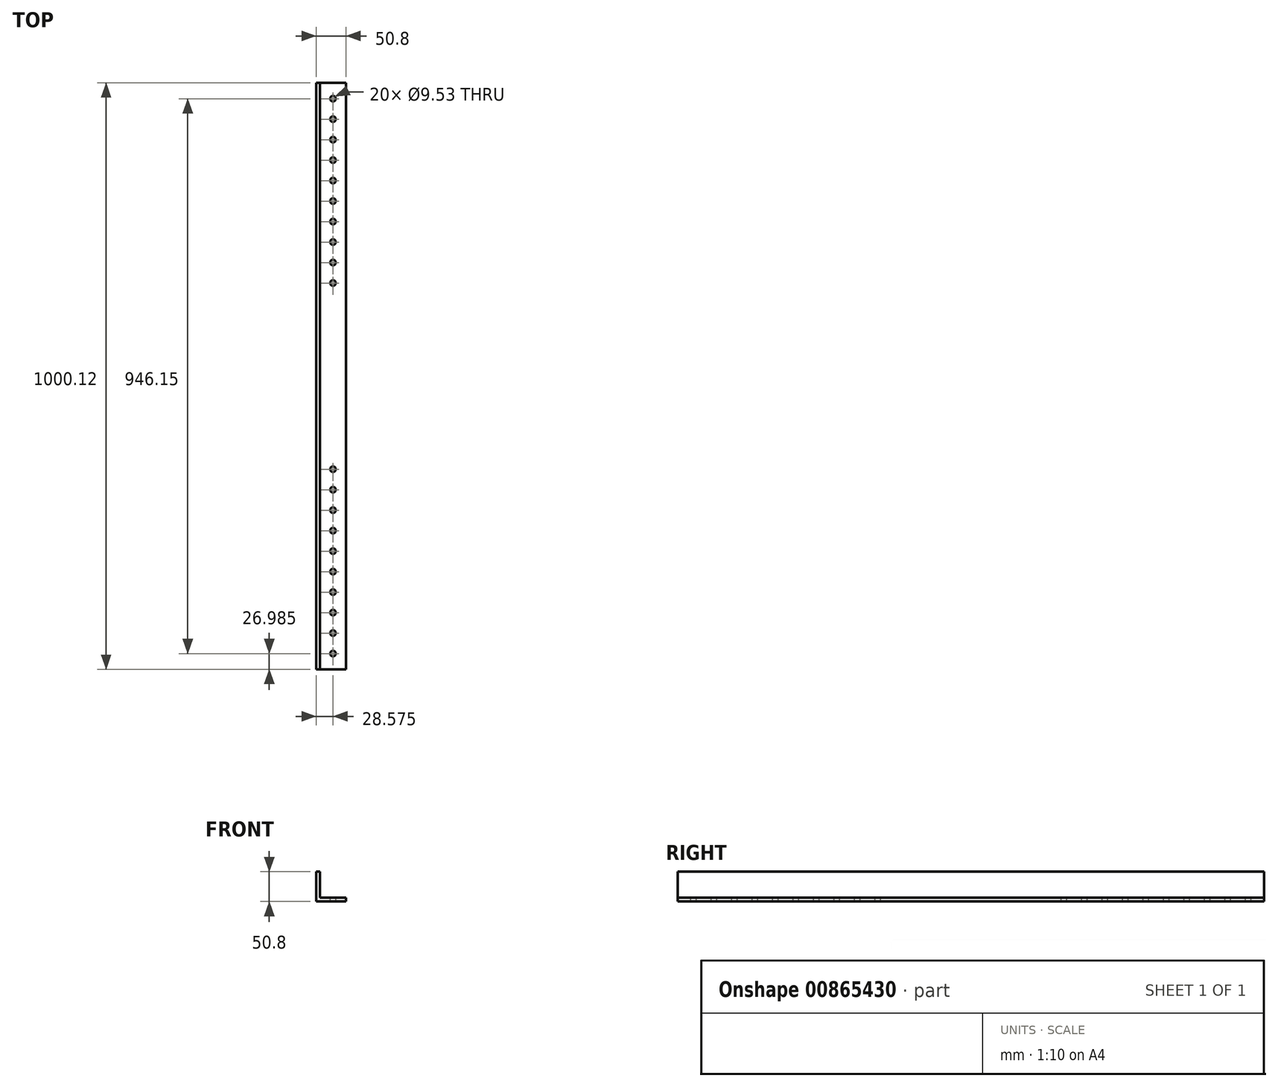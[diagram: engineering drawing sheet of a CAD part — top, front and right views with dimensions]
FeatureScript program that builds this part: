
annotation { "Feature Type Name" : "Feature", "Feature Type Description" : "" }
export const myFeature = defineFeature(function(context is Context, id is Id, definition is map)
    precondition{}
    {
        {
            var Q0;
            Q0=qCreatedBy(makeId("Front.planeOp"),FACE);
            var sketch = newSketch(context, id + "F0", { "sketchPlane" : qUnion([Q0])});
            skLineSegment(sketch, "E0", {"start": v(0, 0) * mm, "end": v(50.8, 0) * mm});
            skLineSegment(sketch, "E1", {"start": v(50.8, 0) * mm, "end": v(50.8, 6.35) * mm});
            skLineSegment(sketch, "E2", {"start": v(50.8, 6.35) * mm, "end": v(6.35, 6.35) * mm});
            skLineSegment(sketch, "E3", {"start": v(6.35, 6.35) * mm, "end": v(6.35, 50.8) * mm});
            skLineSegment(sketch, "E4", {"start": v(6.35, 50.8) * mm, "end": v(0, 50.8) * mm});
            skLineSegment(sketch, "E5", {"start": v(0, 50.8) * mm, "end": v(0, 0) * mm});
            skSolve(sketch);
        }
        {
            var Q0;
            Q0=makeQuery(id+"F0.imprint","IMPRINT",FACE,{"disambiguationData":[TD([[makeQuery(id+"F0.imprint","IMPRINT",EDGE,{"derivedFrom":sQuery(id+"F0.wireOp",EDGE,"E0")}),1.0]])]});
            extrude(context, id + "F1", {"entities" : qUnion([Q0]), "endBound" : BoundingType.SYMMETRIC, "depth" : 1000.12 * mm, "offsetDistance" : 25.4 * mm});
        }
        {
            var Q0;
            Q0=makeQuery(id+"F1.opExtrude","SWEPT_FACE",FACE,{"disambiguationData":[OSD([sQuery(id+"F0.wireOp",EDGE,"E2")])]});
            var sketch = newSketch(context, id + "F2", { "sketchPlane" : qUnion([Q0])});
            skLineSegment(sketch, "E6", {"start": v(28.58, 500.06) * mm, "end": v(28.58, -500.06) * mm, "construction": true});
            skCircle(sketch, "E7", {"center": v(28.58, 473.08) * mm, "radius": 4.76 * mm});
            skCircle(sketch, "E8.0.1.0", {"center": v(28.58, 438.15) * mm, "radius": 4.76 * mm});
            skCircle(sketch, "E8.0.2.0", {"center": v(28.58, 403.23) * mm, "radius": 4.76 * mm});
            skCircle(sketch, "E8.0.3.0", {"center": v(28.58, 368.3) * mm, "radius": 4.76 * mm});
            skCircle(sketch, "E8.0.4.0", {"center": v(28.58, 333.38) * mm, "radius": 4.76 * mm});
            skCircle(sketch, "E8.0.5.0", {"center": v(28.58, 298.45) * mm, "radius": 4.76 * mm});
            skCircle(sketch, "E8.0.6.0", {"center": v(28.58, 263.52) * mm, "radius": 4.76 * mm});
            skCircle(sketch, "E8.0.7.0", {"center": v(28.58, 228.6) * mm, "radius": 4.76 * mm});
            skCircle(sketch, "E8.0.8.0", {"center": v(28.58, 193.67) * mm, "radius": 4.76 * mm});
            skCircle(sketch, "E8.0.9.0", {"center": v(28.58, 158.75) * mm, "radius": 4.76 * mm});
            skLineSegment(sketch, "E8.direction1", {"start": v(28.58, 473.08) * mm, "end": v(53.98, 473.08) * mm, "construction": true});
            skLineSegment(sketch, "E8.direction2", {"start": v(28.58, 473.08) * mm, "end": v(28.58, 438.15) * mm, "construction": true});
            skCircle(sketch, "E9.MirrorC", {"center": v(28.58, -158.75) * mm, "radius": 4.76 * mm});
            skCircle(sketch, "E10.MirrorC", {"center": v(28.58, -193.67) * mm, "radius": 4.76 * mm});
            skCircle(sketch, "E11.MirrorC", {"center": v(28.58, -228.6) * mm, "radius": 4.76 * mm});
            skCircle(sketch, "E12.MirrorC", {"center": v(28.58, -263.52) * mm, "radius": 4.76 * mm});
            skCircle(sketch, "E13.MirrorC", {"center": v(28.58, -298.45) * mm, "radius": 4.76 * mm});
            skCircle(sketch, "E14.MirrorC", {"center": v(28.58, -333.38) * mm, "radius": 4.76 * mm});
            skCircle(sketch, "E15.MirrorC", {"center": v(28.58, -473.08) * mm, "radius": 4.76 * mm});
            skCircle(sketch, "E16.MirrorC", {"center": v(28.58, -438.15) * mm, "radius": 4.76 * mm});
            skCircle(sketch, "E17.MirrorC", {"center": v(28.58, -403.23) * mm, "radius": 4.76 * mm});
            skCircle(sketch, "E18.MirrorC", {"center": v(28.58, -368.3) * mm, "radius": 4.76 * mm});
            skSolve(sketch);
        }
        {
            var Q0;
            Q0 = qSketchRegion(id + "F2", true);
            extrude(context, id + "F3", {"entities" : qUnion([Q0]), "operationType" : NewBodyOperationType.REMOVE, "endBound" : BoundingType.THROUGH_ALL, "oppositeDirection" : true, "depth" : 25.4 * mm, "offsetDistance" : 25.4 * mm});
        }
    });
